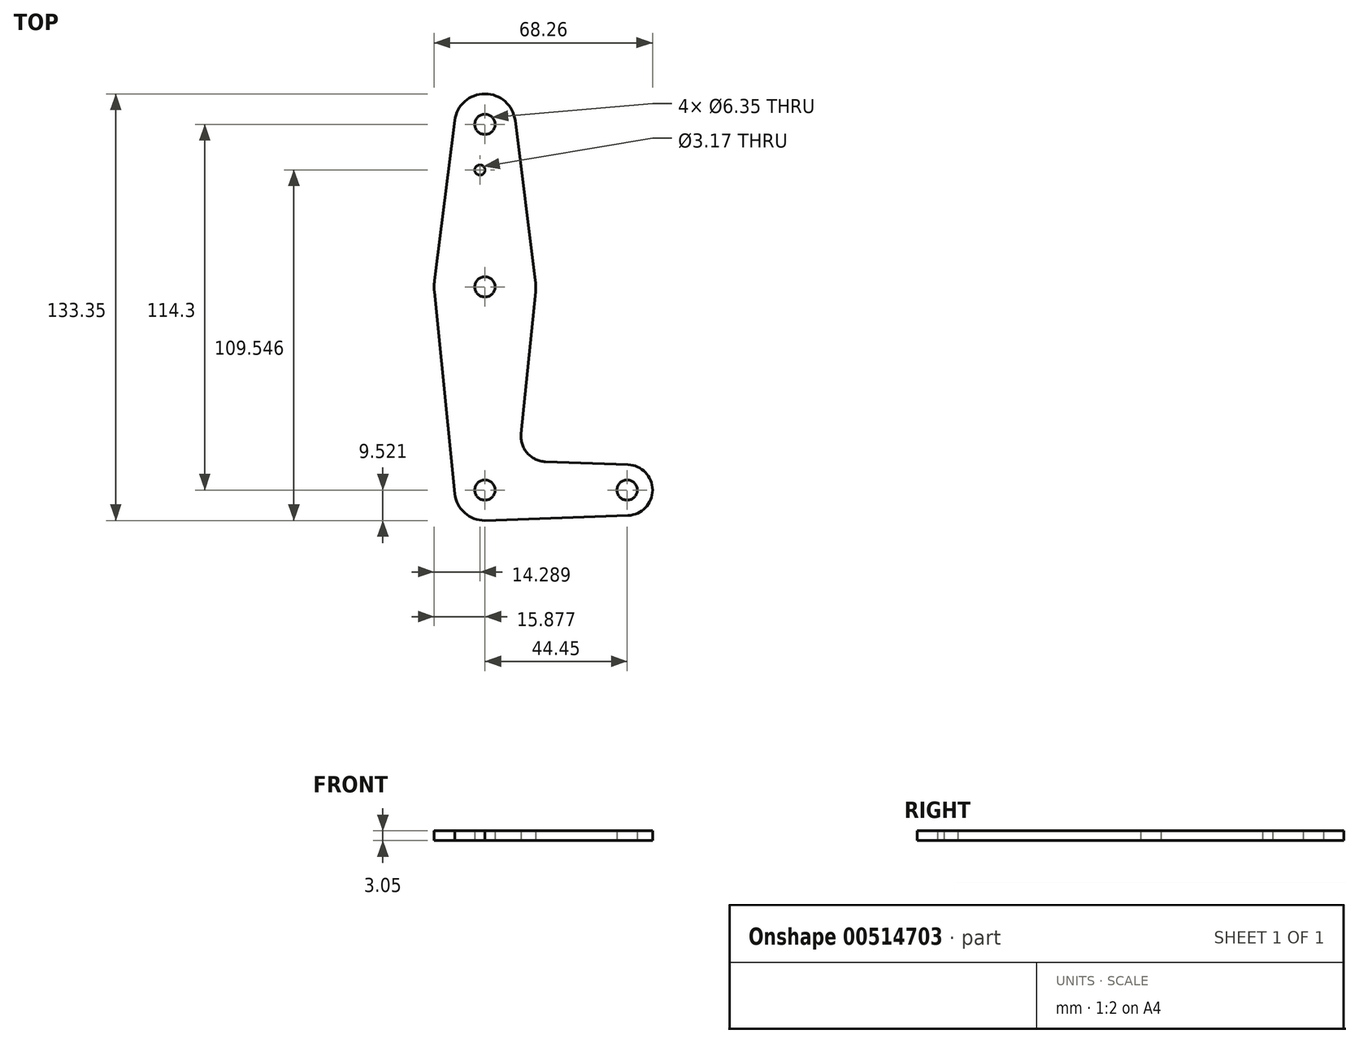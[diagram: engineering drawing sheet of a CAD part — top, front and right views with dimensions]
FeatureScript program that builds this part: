
annotation { "Feature Type Name" : "Feature", "Feature Type Description" : "" }
export const myFeature = defineFeature(function(context is Context, id is Id, definition is map)
    precondition{}
    {
        {
            var Q0;
            Q0=qCreatedBy(makeId("Top.planeOp"),FACE);
            var sketch = newSketch(context, id + "F0", { "sketchPlane" : qUnion([Q0])});
            skLineSegment(sketch, "E0", {"start": v(-36.21, 84.63) * mm, "end": v(-36.21, -29.67) * mm, "construction": true});
            skLineSegment(sketch, "E1", {"start": v(-36.21, -29.67) * mm, "end": v(8.24, -29.67) * mm, "construction": true});
            skCircle(sketch, "E2", {"center": v(-36.21, 84.63) * mm, "radius": 9.53 * mm});
            skCircle(sketch, "E3", {"center": v(-36.21, 33.83) * mm, "radius": 15.88 * mm});
            skCircle(sketch, "E4", {"center": v(-36.21, -29.67) * mm, "radius": 9.53 * mm});
            skCircle(sketch, "E5", {"center": v(8.24, -29.67) * mm, "radius": 7.94 * mm});
            skLineSegment(sketch, "E6", {"start": v(-51.96, 35.82) * mm, "end": v(-45.66, 85.82) * mm});
            skLineSegment(sketch, "E7", {"start": v(-20.46, 35.82) * mm, "end": v(-26.76, 85.82) * mm});
            skLineSegment(sketch, "E8", {"start": v(-45.66, -30.86) * mm, "end": v(-52, 32.24) * mm});
            skLineSegment(sketch, "E9", {"start": v(-24.9, -12.07) * mm, "end": v(-20.42, 32.24) * mm});
            skLineSegment(sketch, "E10", {"start": v(-36.21, -39.2) * mm, "end": v(8.52, -37.6) * mm});
            skLineSegment(sketch, "E11", {"start": v(8.52, -21.74) * mm, "end": v(-17.28, -20.81) * mm});
            skCircle(sketch, "E12", {"center": v(-37.8, 70.36) * mm, "radius": 1.59 * mm});
            skCircle(sketch, "E13", {"center": v(-36.21, 33.83) * mm, "radius": 3.18 * mm});
            skCircle(sketch, "E14", {"center": v(-36.21, -29.67) * mm, "radius": 3.18 * mm});
            skCircle(sketch, "E15", {"center": v(8.24, -29.67) * mm, "radius": 3.18 * mm});
            skCircle(sketch, "E16", {"center": v(-36.21, 84.63) * mm, "radius": 3.18 * mm});
            skPoint(sketch, "E17.newPointA", {"position": v(-36.21, -20.14) * mm});
            skArc(sketch, "E17.filletArc", {"start": v(-24.9, -12.07) * mm, "mid": v(-22.99, -18.1) * mm, "end": v(-17.28, -20.81) * mm});
            skSolve(sketch);
        }
        {
            var Q0;
            Q0=makeQuery(id+"F0.imprint","IMPRINT",FACE,{"disambiguationData":[TD([[makeQuery(id+"F0.imprint","IMPRINT",EDGE,{"derivedFrom":sQuery(id+"F0.wireOp",EDGE,"E15")}),-1.0]])]});
            var Q1;
            {var subQ5=sQuery(id+"F0.wireOp",EDGE,"E9");Q1=makeQuery(id+"F0.imprint","IMPRINT",FACE,{"disambiguationData":[TD([[makeQuery(id+"F0.imprint","IMPRINT",EDGE,{"derivedFrom":subQ5}),1.0]])]});}
            var Q2;
            Q2=makeQuery(id+"F0.imprint","IMPRINT",FACE,{"disambiguationData":[TD([[makeQuery(id+"F0.imprint","IMPRINT",EDGE,{"derivedFrom":sQuery(id+"F0.wireOp",EDGE,"E14")}),-1.0]])]});
            var Q3;
            Q3=makeQuery(id+"F0.imprint","IMPRINT",FACE,{"disambiguationData":[TD([[makeQuery(id+"F0.imprint","IMPRINT",EDGE,{"derivedFrom":sQuery(id+"F0.wireOp",EDGE,"E13")}),-1.0]])]});
            var Q4;
            {var subQ1=sQuery(id+"F0.wireOp",EDGE,"E6");Q4=makeQuery(id+"F0.imprint","IMPRINT",FACE,{"disambiguationData":[TD([[makeQuery(id+"F0.imprint","IMPRINT",EDGE,{"derivedFrom":subQ1}),-1.0]])]});}
            var Q5;
            Q5=makeQuery(id+"F0.imprint","IMPRINT",FACE,{"disambiguationData":[TD([[makeQuery(id+"F0.imprint","IMPRINT",EDGE,{"derivedFrom":sQuery(id+"F0.wireOp",EDGE,"E16")}),-1.0]])]});
            extrude(context, id + "F1", {"entities" : qUnion([Q0, Q1, Q2, Q3, Q4, Q5]), "depth" : 3.05 * mm, "offsetDistance" : 25.4 * mm});
        }
    });
